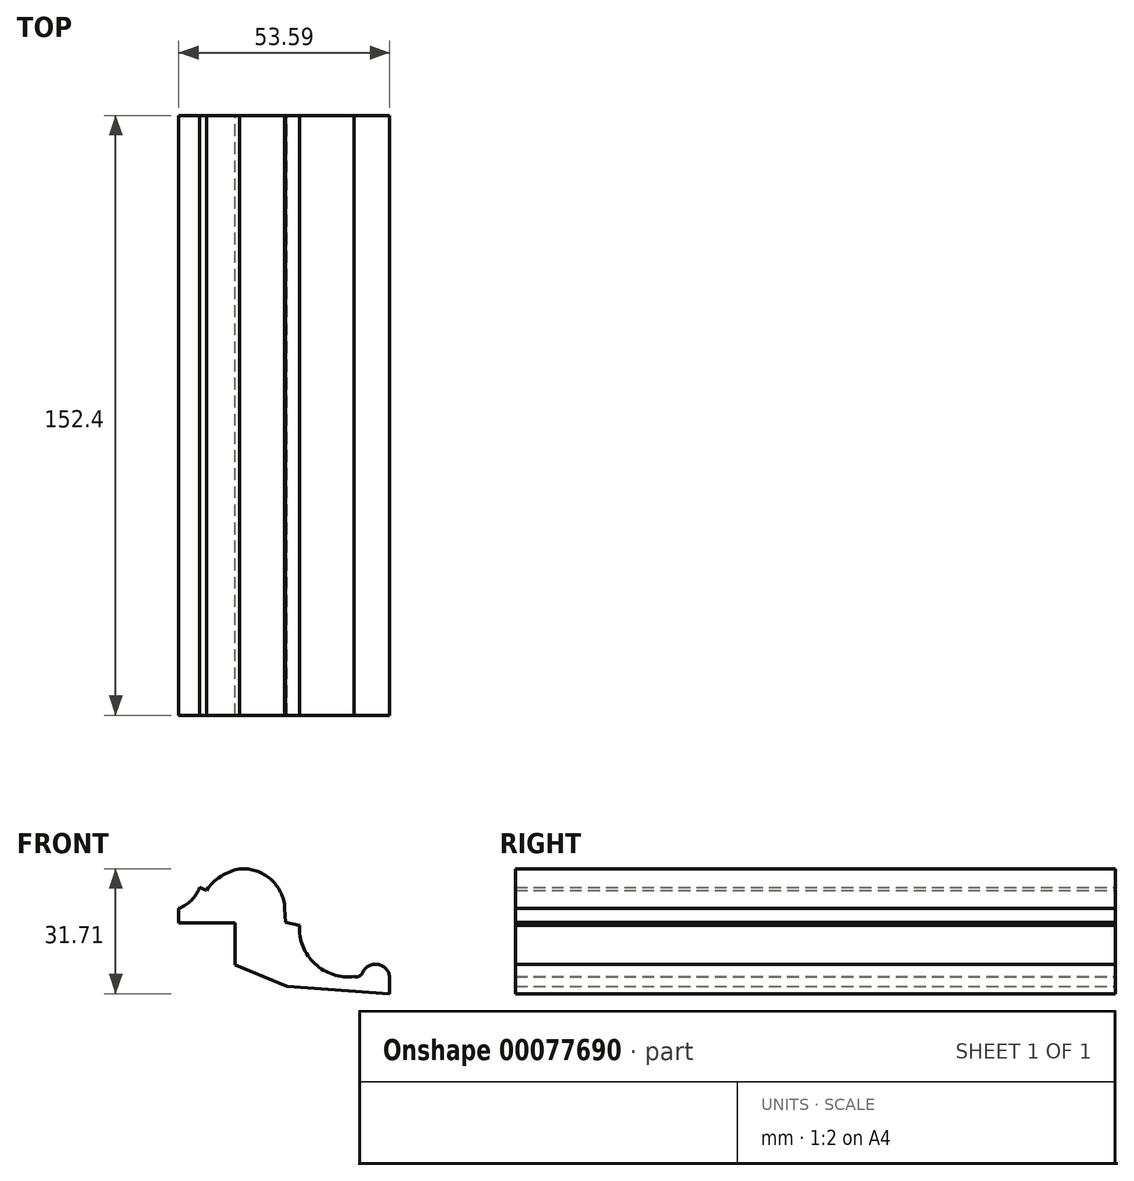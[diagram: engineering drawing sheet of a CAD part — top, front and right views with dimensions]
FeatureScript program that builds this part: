
annotation { "Feature Type Name" : "Feature", "Feature Type Description" : "" }
export const myFeature = defineFeature(function(context is Context, id is Id, definition is map)
    precondition{}
    {
        {
            var Q0;
            Q0=qCreatedBy(makeId("Front.planeOp"),FACE);
            var sketch = newSketch(context, id + "F0", { "sketchPlane" : qUnion([Q0])});
            skLineSegment(sketch, "E0", {"start": v(-26.8, 5.75) * mm, "end": v(-26.8, 2.18) * mm});
            skLineSegment(sketch, "E1", {"start": v(-26.8, 2.18) * mm, "end": v(-12.5, 2.18) * mm});
            skLineSegment(sketch, "E2", {"start": v(-12.5, 2.18) * mm, "end": v(-12.5, -8.54) * mm});
            skArc(sketch, "E3", {"start": v(-26.8, 5.75) * mm, "mid": v(-23.58, 7.89) * mm, "end": v(-21.44, 11.1) * mm});
            skLineSegment(sketch, "E4", {"start": v(-21.44, 11.1) * mm, "end": v(-19.79, 10.42) * mm});
            skArc(sketch, "E5", {"start": v(-11.32, 15.81) * mm, "mid": v(-16.1, 13.97) * mm, "end": v(-19.79, 10.42) * mm});
            skArc(sketch, "E6", {"start": v(0.15, 5.86) * mm, "mid": v(-3.48, 13.26) * mm, "end": v(-11.32, 15.81) * mm});
            skLineSegment(sketch, "E7", {"start": v(0.15, 5.86) * mm, "end": v(0.4, 2.19) * mm});
            skLineSegment(sketch, "E8", {"start": v(0.4, 2.19) * mm, "end": v(3.9, 1.45) * mm});
            skLineSegment(sketch, "E9", {"start": v(-12.5, -8.54) * mm, "end": v(0.7, -14.01) * mm});
            skLineSegment(sketch, "E10", {"start": v(0.7, -14.01) * mm, "end": v(26.8, -15.86) * mm});
            skLineSegment(sketch, "E11", {"start": v(26.8, -15.86) * mm, "end": v(26.8, -11.95) * mm});
            skArc(sketch, "E12", {"start": v(26.8, -11.95) * mm, "mid": v(25.75, -9.42) * mm, "end": v(23.22, -8.38) * mm});
            skArc(sketch, "E13", {"start": v(23.22, -8.38) * mm, "mid": v(21.27, -8.96) * mm, "end": v(19.95, -10.52) * mm});
            skArc(sketch, "E14", {"start": v(3.9, 1.45) * mm, "mid": v(7.8, -8.27) * mm, "end": v(17.77, -11.5) * mm});
            skArc(sketch, "E15", {"start": v(17.77, -11.5) * mm, "mid": v(19.05, -11.43) * mm, "end": v(19.95, -10.52) * mm});
            skSolve(sketch);
        }
        {
            var Q0;
            Q0=makeQuery(id+"F0.imprint","IMPRINT",FACE,{"disambiguationData":[TD([[makeQuery(id+"F0.imprint","IMPRINT",EDGE,{"derivedFrom":sQuery(id+"F0.wireOp",EDGE,"E0")}),1.0]])]});
            extrude(context, id + "F1", {"entities" : qUnion([Q0]), "depth" : 152.4 * mm});
        }
    });
